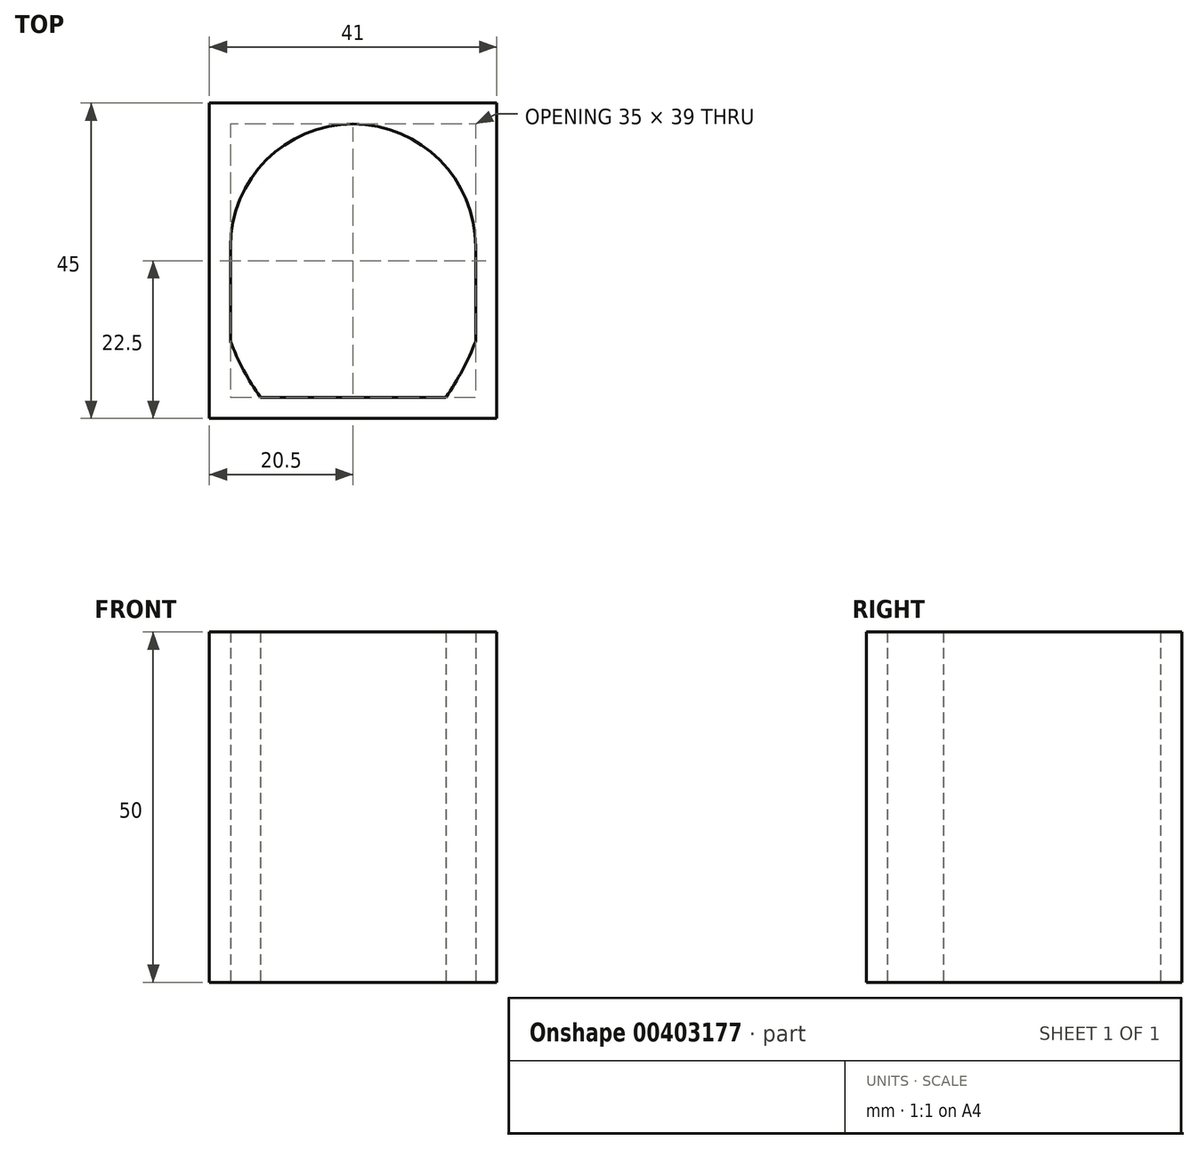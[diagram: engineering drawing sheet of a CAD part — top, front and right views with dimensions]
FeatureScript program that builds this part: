
annotation { "Feature Type Name" : "Feature", "Feature Type Description" : "" }
export const myFeature = defineFeature(function(context is Context, id is Id, definition is map)
    precondition{}
    {
        {
            var Q0;
            Q0=qCreatedBy(makeId("Top.planeOp"),FACE);
            var sketch = newSketch(context, id + "F0", { "sketchPlane" : qUnion([Q0])});
            skLineSegment(sketch, "E0", {"start": v(35, 8) * mm, "end": v(35, 21.5) * mm});
            skLineSegment(sketch, "E1", {"start": v(0, 21.5) * mm, "end": v(0, 8) * mm});
            skLineSegment(sketch, "E2", {"start": v(17.5, 21.5) * mm, "end": v(17.5, 21.3) * mm});
            skPoint(sketch, "E2.endSnap0", {"position": v(17.5, 21.5) * mm});
            skArc(sketch, "E3", {"start": v(35, 21.5) * mm, "mid": v(17.5, 39) * mm, "end": v(0, 21.5) * mm});
            skPoint(sketch, "E4.orphan", {"position": v(35, 39) * mm});
            skPoint(sketch, "E5.orphan", {"position": v(0, 39) * mm});
            skPoint(sketch, "E6.orphan", {"position": v(17.5, 39) * mm});
            skArc(sketch, "E7", {"start": v(30.74, 0) * mm, "mid": v(33.11, 3.87) * mm, "end": v(35, 8) * mm});
            skArc(sketch, "E8", {"start": v(0, 8) * mm, "mid": v(1.89, 3.87) * mm, "end": v(4.26, 0) * mm});
            skPoint(sketch, "E9.end.orphan", {"position": v(0, 8) * mm});
            skLineSegment(sketch, "E10", {"start": v(4.26, 0) * mm, "end": v(30.74, 0) * mm});
            skLineSegment(sketch, "E11", {"start": v(-3, -3) * mm, "end": v(-3, 42) * mm});
            skLineSegment(sketch, "E12", {"start": v(30.74, -3) * mm, "end": v(-3, -3) * mm});
            skLineSegment(sketch, "E13", {"start": v(38, 8) * mm, "end": v(38, 42) * mm});
            skLineSegment(sketch, "E14", {"start": v(17.5, 42) * mm, "end": v(38, 42) * mm});
            skLineSegment(sketch, "E15", {"start": v(17.5, 42) * mm, "end": v(-3, 42) * mm});
            skLineSegment(sketch, "E16", {"start": v(38, 8) * mm, "end": v(38, -3) * mm});
            skLineSegment(sketch, "E17", {"start": v(30.74, -3) * mm, "end": v(38, -3) * mm});
            skSolve(sketch);
        }
        {
            var Q0;
            Q0=makeQuery(id+"F0.imprint","IMPRINT",FACE,{"disambiguationData":[TD([[makeQuery(id+"F0.imprint","IMPRINT",EDGE,{"derivedFrom":sQuery(id+"F0.wireOp",EDGE,"E0")}),-1.0]])]});
            extrude(context, id + "F1", {"entities" : qUnion([Q0]), "depth" : 50 * mm});
        }
    });
